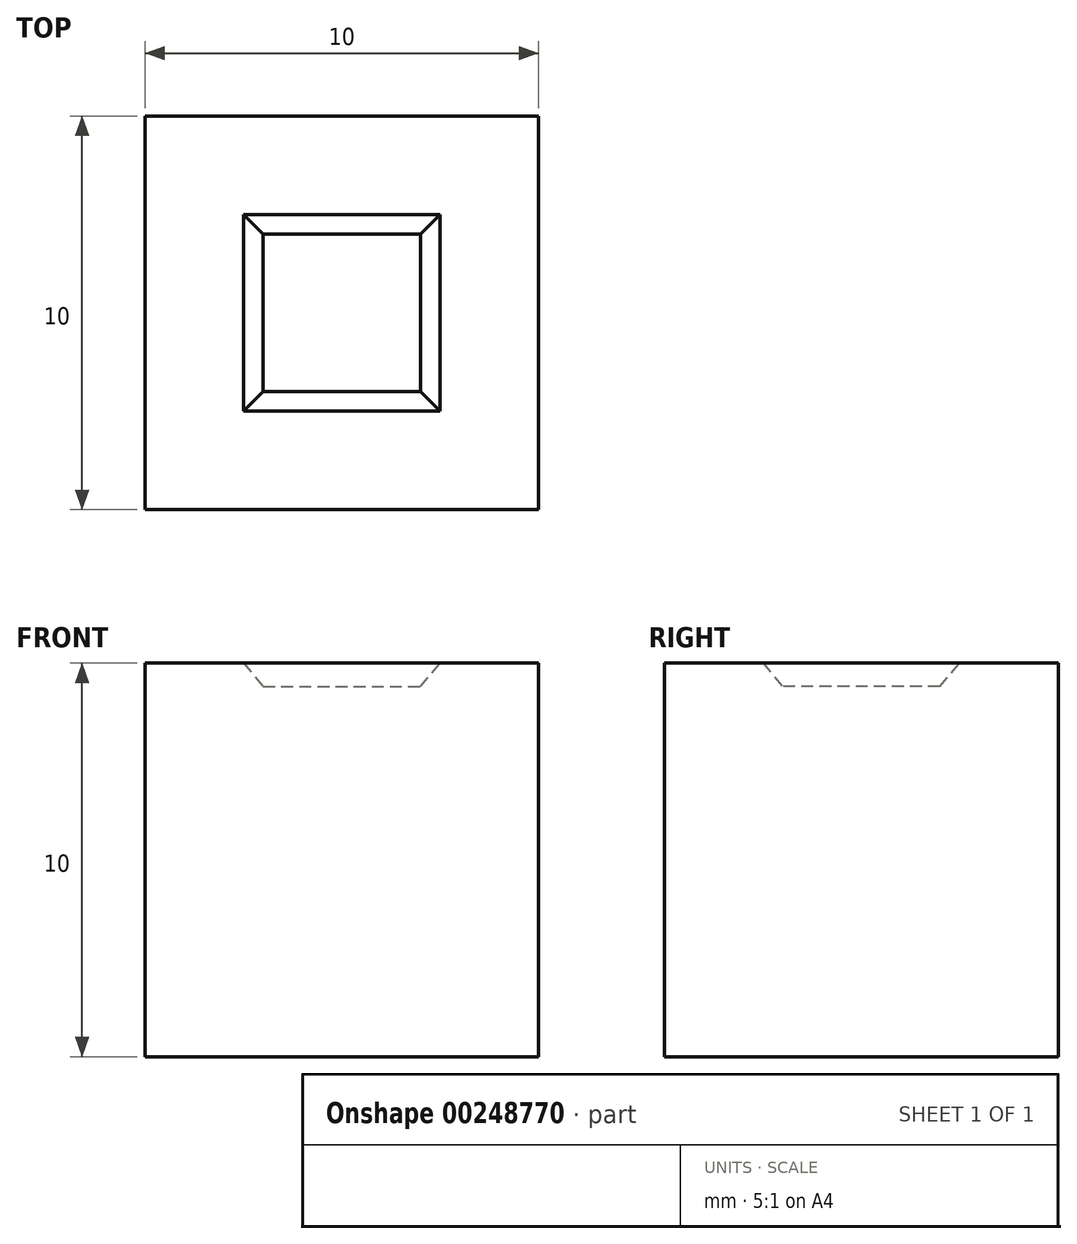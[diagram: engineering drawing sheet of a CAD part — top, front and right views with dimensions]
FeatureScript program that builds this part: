
annotation { "Feature Type Name" : "Feature", "Feature Type Description" : "" }
export const myFeature = defineFeature(function(context is Context, id is Id, definition is map)
    precondition{}
    {
        {
            var Q0;
            Q0=qCreatedBy(makeId("Top.planeOp"),FACE);
            var sketch = newSketch(context, id + "F0", { "sketchPlane" : qUnion([Q0])});
            skLineSegment(sketch, "E0.bottom", {"start": v(-5, -5) * mm, "end": v(5, -5) * mm});
            skLineSegment(sketch, "E0.top", {"start": v(-5, 5) * mm, "end": v(5, 5) * mm});
            skLineSegment(sketch, "E0.left", {"start": v(-5, -5) * mm, "end": v(-5, 5) * mm});
            skLineSegment(sketch, "E0.right", {"start": v(5, -5) * mm, "end": v(5, 5) * mm});
            skSolve(sketch);
        }
        {
            var Q0;
            Q0=makeQuery(id+"F0.imprint","IMPRINT",FACE,{"disambiguationData":[TD([[makeQuery(id+"F0.imprint","IMPRINT",EDGE,{"derivedFrom":sQuery(id+"F0.wireOp",EDGE,"E0.bottom")}),1.0]])]});
            extrude(context, id + "F1", {"entities" : qUnion([Q0]), "depth" : 10 * mm});
        }
        {
            var Q0;
            Q0=makeQuery(id+"F1.opExtrude","CAP_FACE",FACE,{"disambiguationData":[OSD([sQuery(id+"F0.wireOp",EDGE,"E0.bottom"),sQuery(id+"F0.wireOp",EDGE,"E0.top"),sQuery(id+"F0.wireOp",EDGE,"E0.left"),sQuery(id+"F0.wireOp",EDGE,"E0.right")])],"isStart":false});
            var sketch = newSketch(context, id + "F2", { "sketchPlane" : qUnion([Q0])});
            skLineSegment(sketch, "E1.bottom", {"start": v(-2.5, -2.5) * mm, "end": v(2.5, -2.5) * mm});
            skLineSegment(sketch, "E1.top", {"start": v(-2.5, 2.5) * mm, "end": v(2.5, 2.5) * mm});
            skLineSegment(sketch, "E1.left", {"start": v(-2.5, -2.5) * mm, "end": v(-2.5, 2.5) * mm});
            skLineSegment(sketch, "E1.right", {"start": v(2.5, -2.5) * mm, "end": v(2.5, 2.5) * mm});
            skSolve(sketch);
        }
        {
            var Q0;
            Q0 = qSketchRegion(id + "F2", true);
            extrude(context, id + "F3", {"entities" : qUnion([Q0]), "operationType" : NewBodyOperationType.REMOVE, "oppositeDirection" : true, "depth" : 0.6 * mm, "hasDraft" : true, "draftAngle" : 40 * degree, "draftPullDirection" : true});
        }
    });
